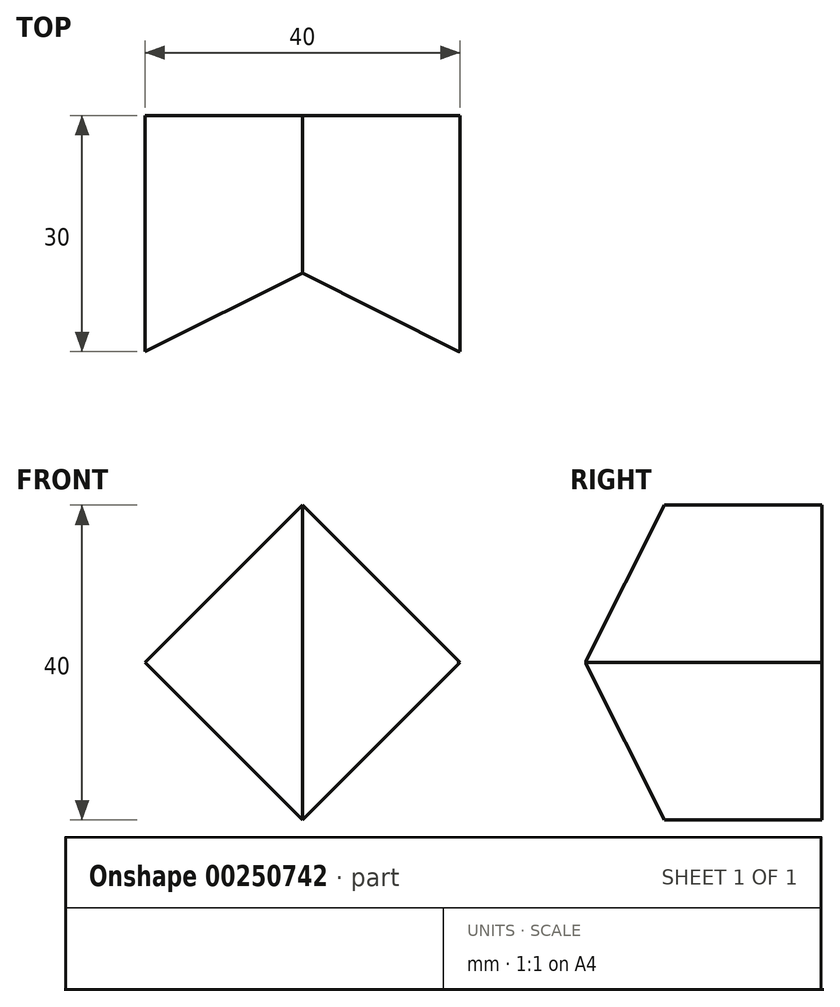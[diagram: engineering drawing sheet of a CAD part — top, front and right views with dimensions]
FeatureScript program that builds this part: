
annotation { "Feature Type Name" : "Feature", "Feature Type Description" : "" }
export const myFeature = defineFeature(function(context is Context, id is Id, definition is map)
    precondition{}
    {
        {
            var Q0;
            Q0=qCreatedBy(makeId("Top.planeOp"),FACE);
            var sketch = newSketch(context, id + "F0", { "sketchPlane" : qUnion([Q0])});
            skLineSegment(sketch, "E0.bottom", {"start": v(0, 0) * mm, "end": v(40, 0) * mm});
            skLineSegment(sketch, "E0.top", {"start": v(0, 30) * mm, "end": v(40, 30) * mm});
            skLineSegment(sketch, "E0.left", {"start": v(0, 0) * mm, "end": v(0, 30) * mm});
            skLineSegment(sketch, "E0.right", {"start": v(40, 0) * mm, "end": v(40, 30) * mm});
            skSolve(sketch);
        }
        {
            var Q0;
            Q0=qCreatedBy(makeId("Front.planeOp"),FACE);
            var sketch = newSketch(context, id + "F1", { "sketchPlane" : qUnion([Q0])});
            skLineSegment(sketch, "E1", {"start": v(0, 0) * mm, "end": v(20, 0) * mm, "construction": true});
            skLineSegment(sketch, "E2", {"start": v(20, 0) * mm, "end": v(20, 40) * mm, "construction": true});
            skLineSegment(sketch, "E3", {"start": v(0, 0) * mm, "end": v(0, 20) * mm, "construction": true});
            skLineSegment(sketch, "E4", {"start": v(0, 20) * mm, "end": v(40, 20) * mm, "construction": true});
            skLineSegment(sketch, "E5", {"start": v(20, 40) * mm, "end": v(0, 20) * mm});
            skLineSegment(sketch, "E6", {"start": v(0, 20) * mm, "end": v(20, 0) * mm});
            skLineSegment(sketch, "E7", {"start": v(40, 20) * mm, "end": v(20, 0) * mm});
            skLineSegment(sketch, "E8", {"start": v(40, 20) * mm, "end": v(20, 40) * mm});
            skLineSegment(sketch, "E9", {"start": v(20, 40) * mm, "end": v(20, 0) * mm});
            skSolve(sketch);
        }
        {
            var Q0;
            Q0 = qSketchRegion(id + "F1", true);
            extrude(context, id + "F2", {"entities" : qUnion([Q0]), "oppositeDirection" : true, "depth" : 30 * mm});
        }
        {
            var Q0;
            Q0=qCreatedBy(makeId("Top.planeOp"),FACE);
            var sketch = newSketch(context, id + "F3", { "sketchPlane" : qUnion([Q0])});
            skLineSegment(sketch, "E10", {"start": v(0, 0) * mm, "end": v(0, 10) * mm, "construction": true});
            skLineSegment(sketch, "E11", {"start": v(0, 10) * mm, "end": v(20, 10) * mm, "construction": true});
            skLineSegment(sketch, "E12", {"start": v(20, 10) * mm, "end": v(20, 0) * mm});
            skSolve(sketch);
        }
        {
            var Q0;
            Q0=qCreatedBy(makeId("Right.planeOp"),FACE);
            var sketch = newSketch(context, id + "F4", { "sketchPlane" : qUnion([Q0])});
            skLineSegment(sketch, "E13", {"start": v(0, 0) * mm, "end": v(10, 0) * mm, "construction": true});
            skLineSegment(sketch, "E14", {"start": v(10, 0) * mm, "end": v(10, 20) * mm, "construction": true});
            skLineSegment(sketch, "E15", {"start": v(10, 20) * mm, "end": v(10.73, 39.99) * mm, "construction": true});
            skSolve(sketch);
        }
        {
            var Q0;
            Q0=makeQuery(id+"F0.imprint","IMPRINT",FACE,{"disambiguationData":[TD([[makeQuery(id+"F0.imprint","IMPRINT",EDGE,{"derivedFrom":sQuery(id+"F0.wireOp",EDGE,"E0.bottom")}),1.0]])]});
            var sketch = newSketch(context, id + "F5", { "sketchPlane" : qUnion([Q0])});
            skLineSegment(sketch, "E16", {"start": v(0, 0) * mm, "end": v(20, 10) * mm});
            skLineSegment(sketch, "E17", {"start": v(20, 10) * mm, "end": v(39.82, 0) * mm});
            skLineSegment(sketch, "E18", {"start": v(39.82, 0) * mm, "end": v(0, 0) * mm});
            skSolve(sketch);
        }
        {
            var Q0;
            Q0=makeQuery(id+"F5.imprint","IMPRINT",FACE,{"disambiguationData":[TD([[makeQuery(id+"F5.imprint","IMPRINT",EDGE,{"derivedFrom":sQuery(id+"F5.wireOp",EDGE,"E16")}),-1.0]])]});
            extrude(context, id + "F6", {"entities" : qUnion([Q0]), "operationType" : NewBodyOperationType.REMOVE, "depth" : 61 * mm});
        }
    });
